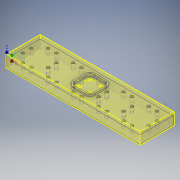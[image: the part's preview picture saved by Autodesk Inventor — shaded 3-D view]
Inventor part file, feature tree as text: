
AUTODESK INVENTOR PART (.ipt)
format: ipt  version: 2018 (Build 220112000, 112)  size: 342,528 bytes
history: native  units: in
note: dims shown in document units (in); Inventor stores cm internally (conversion verified against a paired STEP export)
features: other x5, sketch x2, extrude x2, pattern_linear x1, projected_geometry x1
ambient origin geometry x8: Origin, YZ Plane, XZ Plane, XY Plane, X Axis, Y Axis, Z Axis, Center Point
bodies: Solid1 (feature_tree)
feature tree (11):
  other  "Case Bottom.ipt"
  sketch  "Sketch1"  dims[d0=12.0in d1=3.0in]
  extrude  "Extrusion1"  Depth=3.0in
  extrude  "Extrusion2"  Depth=0.3937in TaperAngle=0.0deg
  pattern_linear  "Rectangular Pattern1"  Spacing1=0.25in  [1 undecoded]
  other  "Solid2::Case Bottom.ipt"
  other  "TaggingFeature1"
  other  "Alignment Sketch"
  other  "Peg Sketch"
  sketch  "Sketch4"  dims[d2=0.3937in d3=0.75in d4=0.0in d5=0.25in d6=0.375in d7=0.5in d8=0.0in d12=1.9685in d14=2.2723in d15=0.3937in d17=0.0in d18=0.115in d19=0.25in d20=0.11in d21=0.375in]
  projected_geometry  "Projected Loop1"
note: 1 required parameter value undecoded (feature->parameter linkage not recoverable at this tier; creation-order binding heuristic only, values carry confidence <= 0.55)
